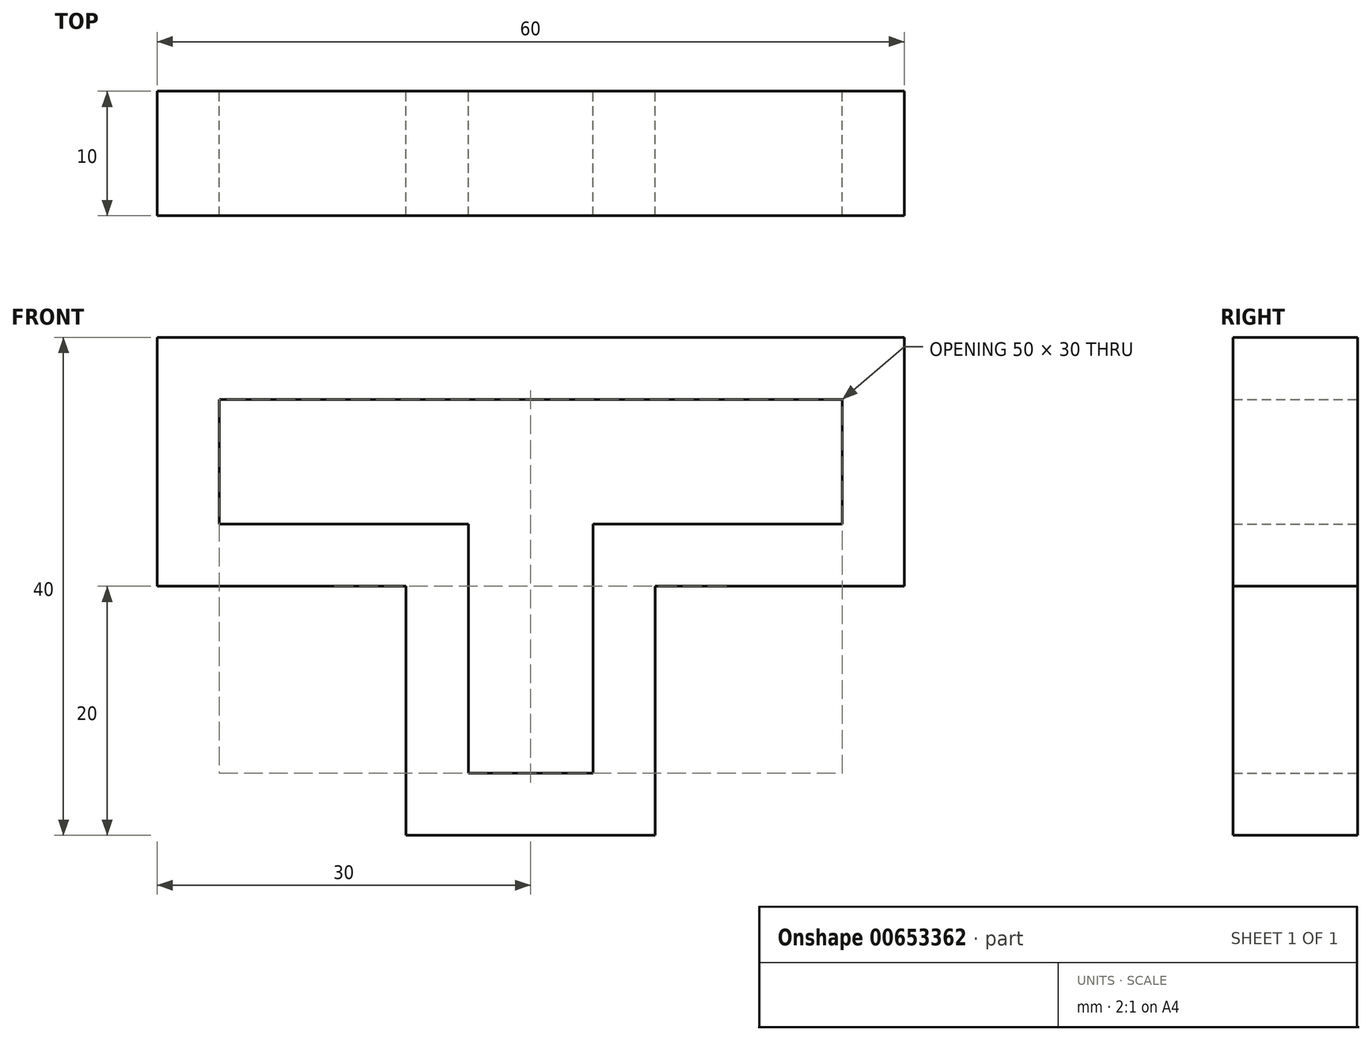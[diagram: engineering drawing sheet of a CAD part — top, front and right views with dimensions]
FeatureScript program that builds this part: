
annotation { "Feature Type Name" : "Feature", "Feature Type Description" : "" }
export const myFeature = defineFeature(function(context is Context, id is Id, definition is map)
    precondition{}
    {
        {
            var Q0;
            Q0=qCreatedBy(makeId("Front.planeOp"),FACE);
            var sketch = newSketch(context, id + "F0", { "sketchPlane" : qUnion([Q0])});
            skLineSegment(sketch, "E0", {"start": v(0, 0) * mm, "end": v(0, 20) * mm});
            skLineSegment(sketch, "E1", {"start": v(0, 20) * mm, "end": v(-20, 20) * mm});
            skLineSegment(sketch, "E2", {"start": v(-20, 20) * mm, "end": v(-20, 40) * mm});
            skLineSegment(sketch, "E3", {"start": v(-20, 40) * mm, "end": v(40, 40) * mm});
            skLineSegment(sketch, "E4", {"start": v(40, 40) * mm, "end": v(40, 20) * mm});
            skLineSegment(sketch, "E5", {"start": v(40, 20) * mm, "end": v(20, 20) * mm});
            skLineSegment(sketch, "E6", {"start": v(20, 20) * mm, "end": v(20, 0) * mm});
            skLineSegment(sketch, "E7", {"start": v(20, 0) * mm, "end": v(0, 0) * mm});
            skLineSegment(sketch, "E8.0", {"start": v(-15, 25) * mm, "end": v(-15, 35) * mm});
            skLineSegment(sketch, "E8.1", {"start": v(5, 25) * mm, "end": v(-15, 25) * mm});
            skLineSegment(sketch, "E8.2", {"start": v(-15, 35) * mm, "end": v(35, 35) * mm});
            skLineSegment(sketch, "E8.3", {"start": v(5, 5) * mm, "end": v(5, 25) * mm});
            skLineSegment(sketch, "E8.4", {"start": v(35, 35) * mm, "end": v(35, 25) * mm});
            skLineSegment(sketch, "E8.5", {"start": v(35, 25) * mm, "end": v(15, 25) * mm});
            skLineSegment(sketch, "E8.6", {"start": v(15, 25) * mm, "end": v(15, 5) * mm});
            skLineSegment(sketch, "E8.7", {"start": v(15, 5) * mm, "end": v(5, 5) * mm});
            skSolve(sketch);
        }
        {
            var Q0;
            Q0=makeQuery(id+"F0.imprint","IMPRINT",FACE,{"disambiguationData":[TD([[makeQuery(id+"F0.imprint","IMPRINT",EDGE,{"derivedFrom":sQuery(id+"F0.wireOp",EDGE,"E0")}),-1.0]])]});
            extrude(context, id + "F1", {"entities" : qUnion([Q0]), "depth" : 10 * mm, "offsetDistance" : 25 * mm});
        }
    });
